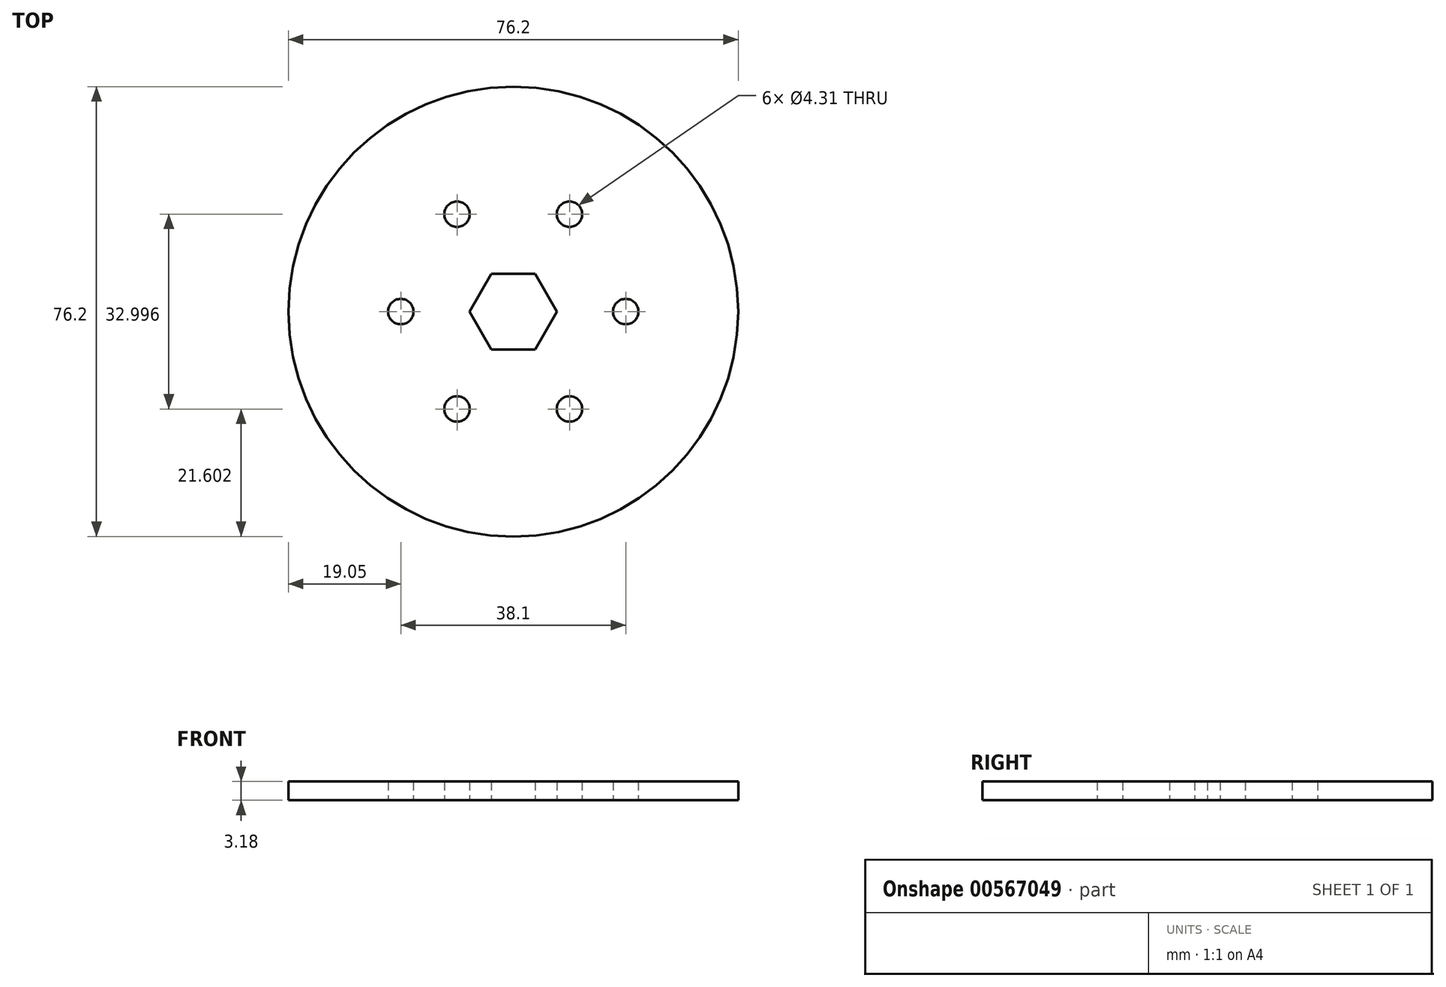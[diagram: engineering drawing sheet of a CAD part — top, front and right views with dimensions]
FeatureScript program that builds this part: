
annotation { "Feature Type Name" : "Feature", "Feature Type Description" : "" }
export const myFeature = defineFeature(function(context is Context, id is Id, definition is map)
    precondition{}
    {
        {
            var Q0;
            Q0=qCreatedBy(makeId("Top.planeOp"),FACE);
            var sketch = newSketch(context, id + "F0", { "sketchPlane" : qUnion([Q0])});
            skCircle(sketch, "E0", {"center": v(0, 0) * mm, "radius": 38.1 * mm});
            skCircle(sketch, "E1", {"center": v(-19.05, 0) * mm, "radius": 2.15 * mm});
            skLineSegment(sketch, "E2", {"start": v(0, 0) * mm, "end": v(-38.1, 0) * mm, "construction": true});
            skLineSegment(sketch, "E3", {"start": v(0, 0) * mm, "end": v(0, 38.1) * mm, "construction": true});
            skLineSegment(sketch, "E4.MirrorCS", {"start": v(0, 0) * mm, "end": v(38.1, 0) * mm, "construction": true});
            skCircle(sketch, "E5.cCircle", {"center": v(0, 0) * mm, "radius": 6.41 * mm, "construction": true});
            skLineSegment(sketch, "E5.0", {"start": v(3.7, -6.41) * mm, "end": v(-3.7, -6.41) * mm});
            skLineSegment(sketch, "E5.1", {"start": v(-3.7, -6.41) * mm, "end": v(-7.4, 0) * mm});
            skLineSegment(sketch, "E5.2", {"start": v(-7.4, 0) * mm, "end": v(-3.7, 6.41) * mm});
            skLineSegment(sketch, "E5.3", {"start": v(-3.7, 6.41) * mm, "end": v(3.7, 6.41) * mm});
            skLineSegment(sketch, "E5.4", {"start": v(3.7, 6.41) * mm, "end": v(7.4, 0) * mm});
            skLineSegment(sketch, "E5.5", {"start": v(7.4, 0) * mm, "end": v(3.7, -6.41) * mm});
            skPoint(sketch, "E5.0.midPoint", {"position": v(0, -6.41) * mm});
            skCircle(sketch, "E6.1.0", {"center": v(-9.53, -16.5) * mm, "radius": 2.15 * mm});
            skCircle(sketch, "E6.2.0", {"center": v(9.52, -16.5) * mm, "radius": 2.15 * mm});
            skCircle(sketch, "E6.3.0", {"center": v(19.05, 0) * mm, "radius": 2.15 * mm});
            skCircle(sketch, "E6.4.0", {"center": v(9.53, 16.5) * mm, "radius": 2.15 * mm});
            skCircle(sketch, "E7.1.5.0", {"center": v(-9.53, 16.5) * mm, "radius": 2.15 * mm});
            skSolve(sketch);
        }
        {
            var Q0;
            Q0=makeQuery(id+"F0.imprint","IMPRINT",FACE,{"disambiguationData":[TD([[makeQuery(id+"F0.imprint","IMPRINT",EDGE,{"derivedFrom":sQuery(id+"F0.wireOp",EDGE,"E0")}),1.0]])]});
            extrude(context, id + "F1", {"entities" : qUnion([Q0]), "depth" : 3.17 * mm, "offsetDistance" : 25.4 * mm});
        }
    });
